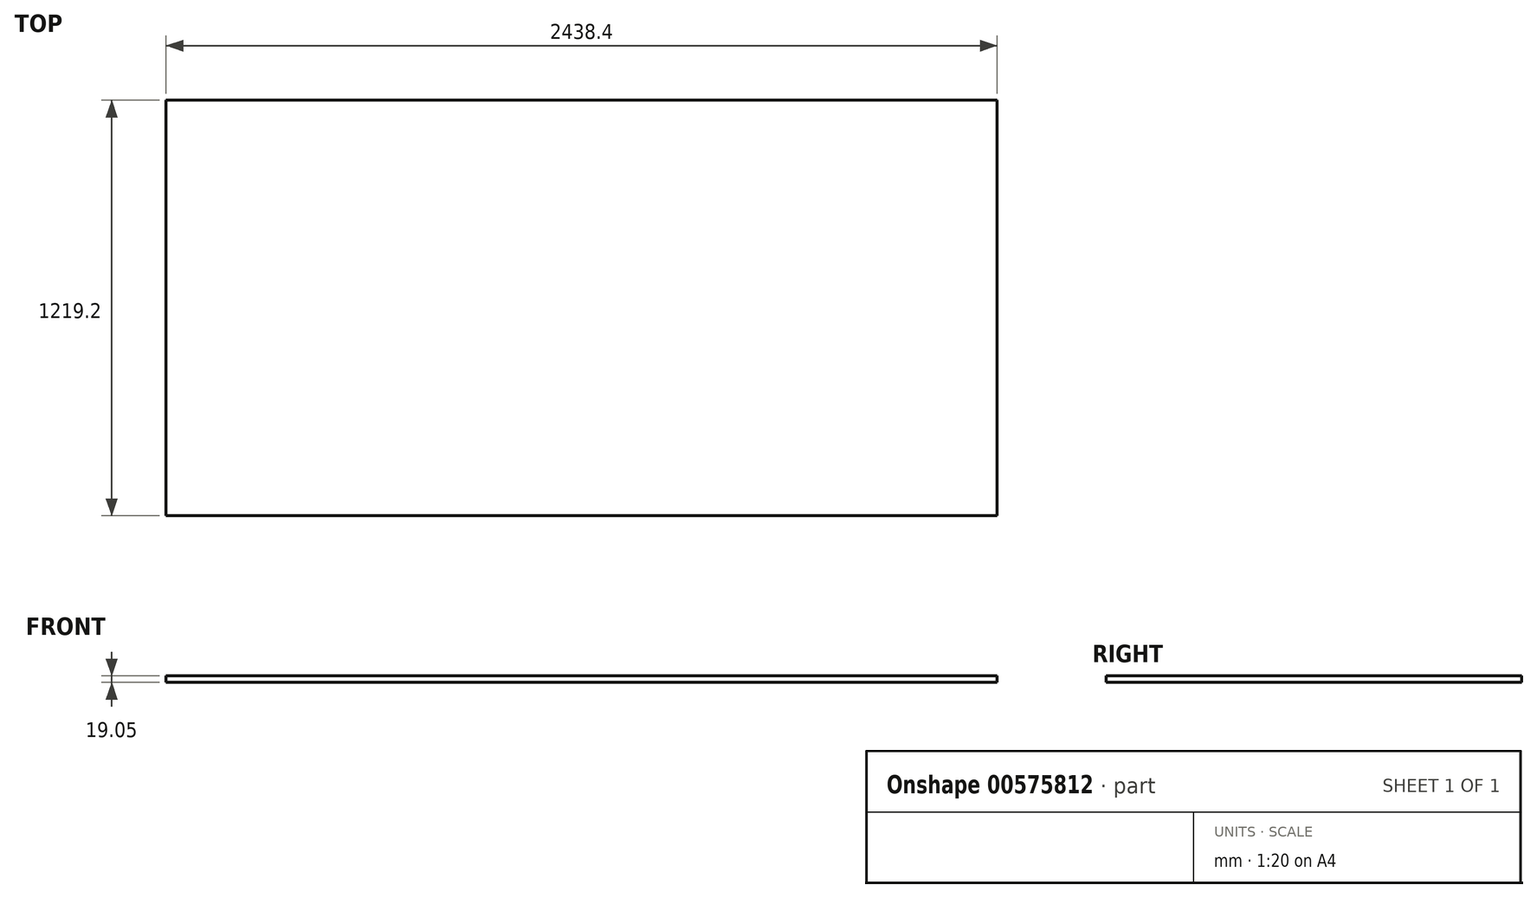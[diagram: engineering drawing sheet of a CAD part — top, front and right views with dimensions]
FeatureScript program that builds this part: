
annotation { "Feature Type Name" : "Feature", "Feature Type Description" : "" }
export const myFeature = defineFeature(function(context is Context, id is Id, definition is map)
    precondition{}
    {
        {
            var Q0;
            Q0=qCreatedBy(makeId("Top.planeOp"),FACE);
            var sketch = newSketch(context, id + "F0", { "sketchPlane" : qUnion([Q0])});
            skLineSegment(sketch, "E0.bottom", {"start": v(98.52, 0) * mm, "end": v(2536.92, 0) * mm});
            skLineSegment(sketch, "E0.top", {"start": v(98.52, 1219.2) * mm, "end": v(2536.92, 1219.2) * mm});
            skLineSegment(sketch, "E0.left", {"start": v(98.52, 0) * mm, "end": v(98.52, 1219.2) * mm});
            skLineSegment(sketch, "E0.right", {"start": v(2536.92, 0) * mm, "end": v(2536.92, 1219.2) * mm});
            skSolve(sketch);
        }
        {
            var Q0;
            Q0=makeQuery(id+"F0.imprint","IMPRINT",FACE,{"disambiguationData":[TD([[makeQuery(id+"F0.imprint","IMPRINT",EDGE,{"derivedFrom":sQuery(id+"F0.wireOp",EDGE,"E0.bottom")}),1.0]])]});
            extrude(context, id + "F1", {"entities" : qUnion([Q0]), "depth" : 19.05 * mm, "offsetDistance" : 25.4 * mm});
        }
    });
